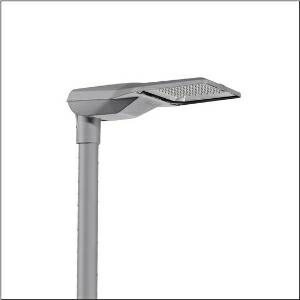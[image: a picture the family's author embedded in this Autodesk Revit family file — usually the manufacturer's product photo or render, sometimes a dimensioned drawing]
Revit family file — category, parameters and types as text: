
# Revit family: streetlight_sl_21_iq_midi___st1_0a_5xe3d31d08mb_825e
name_source: partatom
category: Lighting Fixtures
units: mm (PartAtom-declared; Revit-internal decimal feet)

## family parameters
Cut with Voids When Loaded = No
Host = Face
Light Source = No
Part Type = Normal
Room Calculation Point = No
Round Connector Dimension = Use Diameter
Shared = No

## types (1)
- --- (1 x LED, 19500 lm, 146.7 W, 3000K)
    Apparent Load = 147 VA
    CIE Flux Codes = 37 72 97 100 100
    Color Rendering = 70
    Color Temperature = 3000K
    Default Elevation = 1800 mm
    Description = Streetlight SL 21 iQ midi, mast luminaire, primary light control with lens, of PMMA, primary optical cover: cover, of toughened safety glass, transparent, light distribution: ST1.0a, light emission: direct distribution, primary light characteristic: asymmetric, installation type: post-top, side-entry, LED, High Power LED, rated luminous flux: 19.500lm, luminous efficacy: 133lm/W, light colour: 730, colour temperature: 3000K, control gear: iQ-Comfort, control: Auto-Match, Temp-Guard, Lumen-Switch, Night-Set, Smart-Wire, Light-Fading, Desk-Remote (wireless, voltage-free reading and setting of iQ features in the workshop via application-optimized NFC function/RFID function), optimised constant luminous flux control (CLO 2.0), pre-setting: linear dimming characteristic, mains connection: 230..240V, AC, 50/60Hz, start of lifetime: 147W, end of service life: 161W, reduction: 62W, luminaire housing, of diecast aluminium, powder-coated, SITECO metallic grey (DB 702S), corrosivity category C5 high according to DIN EN ISO 12944, please order mast flange separately, inclination adjustable: 0°, 5°, 10°, 15°, sealing non-destructively replaceable, multi-level sealing system, length: 644mm, width: 335mm, height: 110mm, mast flange for spigot size: 42mm (side-entry): 5XC10008XM4, 60/48mm (side-entry/post-top): 5XC10108XM2, 76/60mm (side-entry/post-top): 5XC10108XM1, mounting height: 4..8m, protection rating (complete): IP66, insulation class (complete): insulation class II (safety insulation), certification: CE, ENEC, ENEC+, VDE, impact resistance: IK10, permissible operating ambient temperature for outdoor applications: -40..+50°C, standard-compliant lighting for roads and squares, packaging unit: 1 piece

Light Distribution: ST1.0a
    Height = 111 mm
    Lamp = 1 x LED
    Lamp Light Flux = 19500 lm
    Lamp Power = 146.7 W
    Lamp count = 1
    Length = 644 mm
    Luminous efficacy = 133 lm/W
    Manufacturer = Siteco
    ModVariant = No
    Model = 5XE3D31D08MB
    Number of Poles = 1
    OnlyDefault = Yes
    Power Factor = 1
    Product Name = Streetlight SL 21 iQ midi | ST1.0a
    Product group = mast luminaire | pylon top
    ProductGroupID = 6100
    Protection Class = Protection class II
    Protection Degree = IP 66
    RLX_Detail_Level = 1
    RLX_Emergency_Light_Flux = 0 lm
    RLX_Emergency_Type = 0
    RLX_Emergency_Type_DB = No
    RlxData = <blob elided: 26905 chars, md5=a3339f74>
    Socket = socket
    Standby Power = 0 W
    System Light Flux = 19499 lm
    System Power = 147 W
    Type Comments = factory setting: luminous flux: 100 % | dim-lin: 254 | 753 mA
    Type Image = l_1004298.jpg
    URL = http://relux.com
    VarID = @adj_186997
    Voltage = 0 V
    Weight = 0.00 kg
    Width = 336 mm

## geometry (parser evidence)
native form markers: Blend x4, Sweep x11
no freeform markers — native parametric forms only
